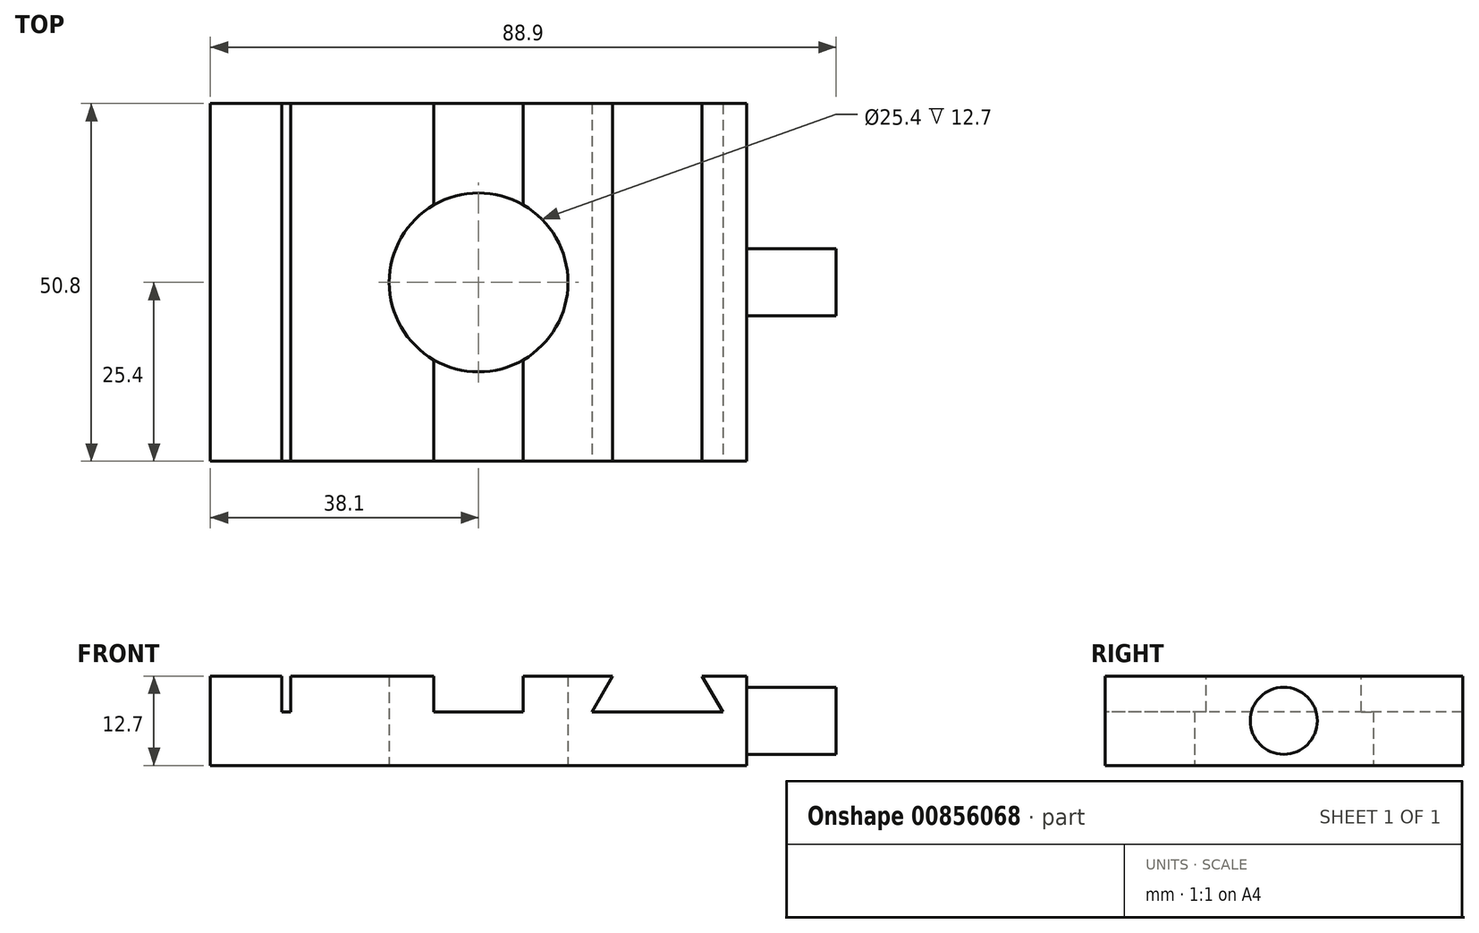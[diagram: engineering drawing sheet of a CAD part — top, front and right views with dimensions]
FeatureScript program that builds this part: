
annotation { "Feature Type Name" : "Feature", "Feature Type Description" : "" }
export const myFeature = defineFeature(function(context is Context, id is Id, definition is map)
    precondition{}
    {
        {
            var Q0;
            Q0=qCreatedBy(makeId("Top.planeOp"),FACE);
            var sketch = newSketch(context, id + "F0", { "sketchPlane" : qUnion([Q0])});
            skLineSegment(sketch, "E0.bottom", {"start": v(38.1, 25.4) * mm, "end": v(-38.1, 25.4) * mm});
            skLineSegment(sketch, "E0.top", {"start": v(38.1, -25.4) * mm, "end": v(-38.1, -25.4) * mm});
            skLineSegment(sketch, "E0.left", {"start": v(38.1, 25.4) * mm, "end": v(38.1, -25.4) * mm});
            skLineSegment(sketch, "E0.right", {"start": v(-38.1, 25.4) * mm, "end": v(-38.1, -25.4) * mm});
            skPoint(sketch, "E0.middle", {"position": v(0, 0) * mm});
            skCircle(sketch, "E1", {"center": v(0, 0) * mm, "radius": 12.7 * mm});
            skSolve(sketch);
        }
        {
            var Q0;
            Q0=makeQuery(id+"F0.imprint","IMPRINT",FACE,{"disambiguationData":[TD([[makeQuery(id+"F0.imprint","IMPRINT",EDGE,{"derivedFrom":sQuery(id+"F0.wireOp",EDGE,"E0.bottom")}),1.0]])]});
            extrude(context, id + "F1", {"entities" : qUnion([Q0]), "depth" : 12.7 * mm, "offsetDistance" : 25.4 * mm});
        }
        {
            var Q0;
            Q0=makeQuery(id+"F1.opExtrude","CAP_FACE",FACE,{"disambiguationData":[OSD([sQuery(id+"F0.wireOp",EDGE,"E0.bottom"),sQuery(id+"F0.wireOp",EDGE,"E0.top"),sQuery(id+"F0.wireOp",EDGE,"E0.left"),sQuery(id+"F0.wireOp",EDGE,"E0.right"),sQuery(id+"F0.wireOp",EDGE,"E1")])],"isStart":false});
            var sketch = newSketch(context, id + "F2", { "sketchPlane" : qUnion([Q0])});
            skLineSegment(sketch, "E2.bottom", {"start": v(-27.94, 25.4) * mm, "end": v(-26.67, 25.4) * mm});
            skLineSegment(sketch, "E2.top", {"start": v(-27.94, -25.4) * mm, "end": v(-26.67, -25.4) * mm});
            skLineSegment(sketch, "E2.left", {"start": v(-27.94, 25.4) * mm, "end": v(-27.94, -25.4) * mm});
            skLineSegment(sketch, "E2.right", {"start": v(-26.67, 25.4) * mm, "end": v(-26.67, -25.4) * mm});
            skLineSegment(sketch, "E3", {"start": v(-6.35, 25.4) * mm, "end": v(-6.35, -25.4) * mm});
            skLineSegment(sketch, "E4", {"start": v(-6.35, -25.4) * mm, "end": v(6.35, -25.4) * mm});
            skLineSegment(sketch, "E5", {"start": v(6.35, -25.4) * mm, "end": v(6.35, 25.4) * mm});
            skLineSegment(sketch, "E6", {"start": v(6.35, 25.4) * mm, "end": v(-6.35, 25.4) * mm});
            skPoint(sketch, "E7", {"position": v(0, 0) * mm});
            skLineSegment(sketch, "E8", {"start": v(0, 25.4) * mm, "end": v(0, -25.4) * mm, "construction": true});
            skSolve(sketch);
        }
        {
            var Q0;
            {var subQ0=sQuery(id+"F2.wireOp",EDGE,"E4");Q0=makeQuery(id+"F2.imprint","IMPRINT",FACE,{"disambiguationData":[TD([[makeQuery(id+"F2.imprint","IMPRINT",EDGE,{"derivedFrom":subQ0}),-1.0]])]});}
            var Q1;
            {var subQ0=sQuery(id+"F2.wireOp",EDGE,"E6");Q1=makeQuery(id+"F2.imprint","IMPRINT",FACE,{"disambiguationData":[TD([[makeQuery(id+"F2.imprint","IMPRINT",EDGE,{"derivedFrom":subQ0}),1.0]])]});}
            var Q2;
            Q2=makeQuery(id+"F2.imprint","IMPRINT",FACE,{"disambiguationData":[TD([[makeQuery(id+"F2.imprint","IMPRINT",EDGE,{"derivedFrom":sQuery(id+"F2.wireOp",EDGE,"E2.bottom")}),1.0]])]});
            extrude(context, id + "F3", {"entities" : qUnion([Q0, Q1, Q2]), "operationType" : NewBodyOperationType.REMOVE, "oppositeDirection" : true, "depth" : 5.08 * mm, "offsetDistance" : 25.4 * mm});
        }
        {
            var Q0;
            Q0=makeQuery(id+"F1.opExtrude","SWEPT_FACE",FACE,{"disambiguationData":[OSD([sQuery(id+"F0.wireOp",EDGE,"E0.top")])]});
            var sketch = newSketch(context, id + "F4", { "sketchPlane" : qUnion([Q0])});
            skLineSegment(sketch, "E9", {"start": v(19.05, 12.7) * mm, "end": v(16.12, 7.62) * mm});
            skLineSegment(sketch, "E10", {"start": v(16.12, 7.62) * mm, "end": v(34.68, 7.62) * mm});
            skLineSegment(sketch, "E11", {"start": v(34.68, 7.62) * mm, "end": v(31.75, 12.7) * mm});
            skLineSegment(sketch, "E12", {"start": v(25.4, 7.62) * mm, "end": v(25.4, 12.7) * mm, "construction": true});
            skSolve(sketch);
        }
        {
            var Q0;
            {var subQ0=sQuery(id+"F4.wireOp",EDGE,"E9");Q0=makeQuery(id+"F4.imprint","IMPRINT",FACE,{"disambiguationData":[TD([[makeQuery(id+"F4.imprint","IMPRINT",EDGE,{"derivedFrom":subQ0}),1.0]])]});}
            extrude(context, id + "F5", {"entities" : qUnion([Q0]), "operationType" : NewBodyOperationType.REMOVE, "endBound" : BoundingType.THROUGH_ALL, "oppositeDirection" : true, "depth" : 25.4 * mm, "offsetDistance" : 25.4 * mm});
        }
        {
            var Q0;
            Q0=makeQuery(id+"F1.opExtrude","SWEPT_FACE",FACE,{"disambiguationData":[OSD([sQuery(id+"F0.wireOp",EDGE,"E0.left")])]});
            var sketch = newSketch(context, id + "F6", { "sketchPlane" : qUnion([Q0])});
            skCircle(sketch, "E13", {"center": v(0, 6.35) * mm, "radius": 4.76 * mm});
            skPoint(sketch, "E13.centerSnap0", {"position": v(-25.4, 6.35) * mm});
            skPoint(sketch, "E13.centerSnap1", {"position": v(0, 12.7) * mm});
            skSolve(sketch);
        }
        {
            var Q0;
            Q0=makeQuery(id+"F6.imprint","IMPRINT",FACE,{"disambiguationData":[TD([[makeQuery(id+"F6.imprint","IMPRINT",EDGE,{"derivedFrom":sQuery(id+"F6.wireOp",EDGE,"E13")}),1.0]])]});
            extrude(context, id + "F7", {"entities" : qUnion([Q0]), "operationType" : NewBodyOperationType.ADD, "depth" : 12.7 * mm, "offsetDistance" : 25.4 * mm});
        }
    });
